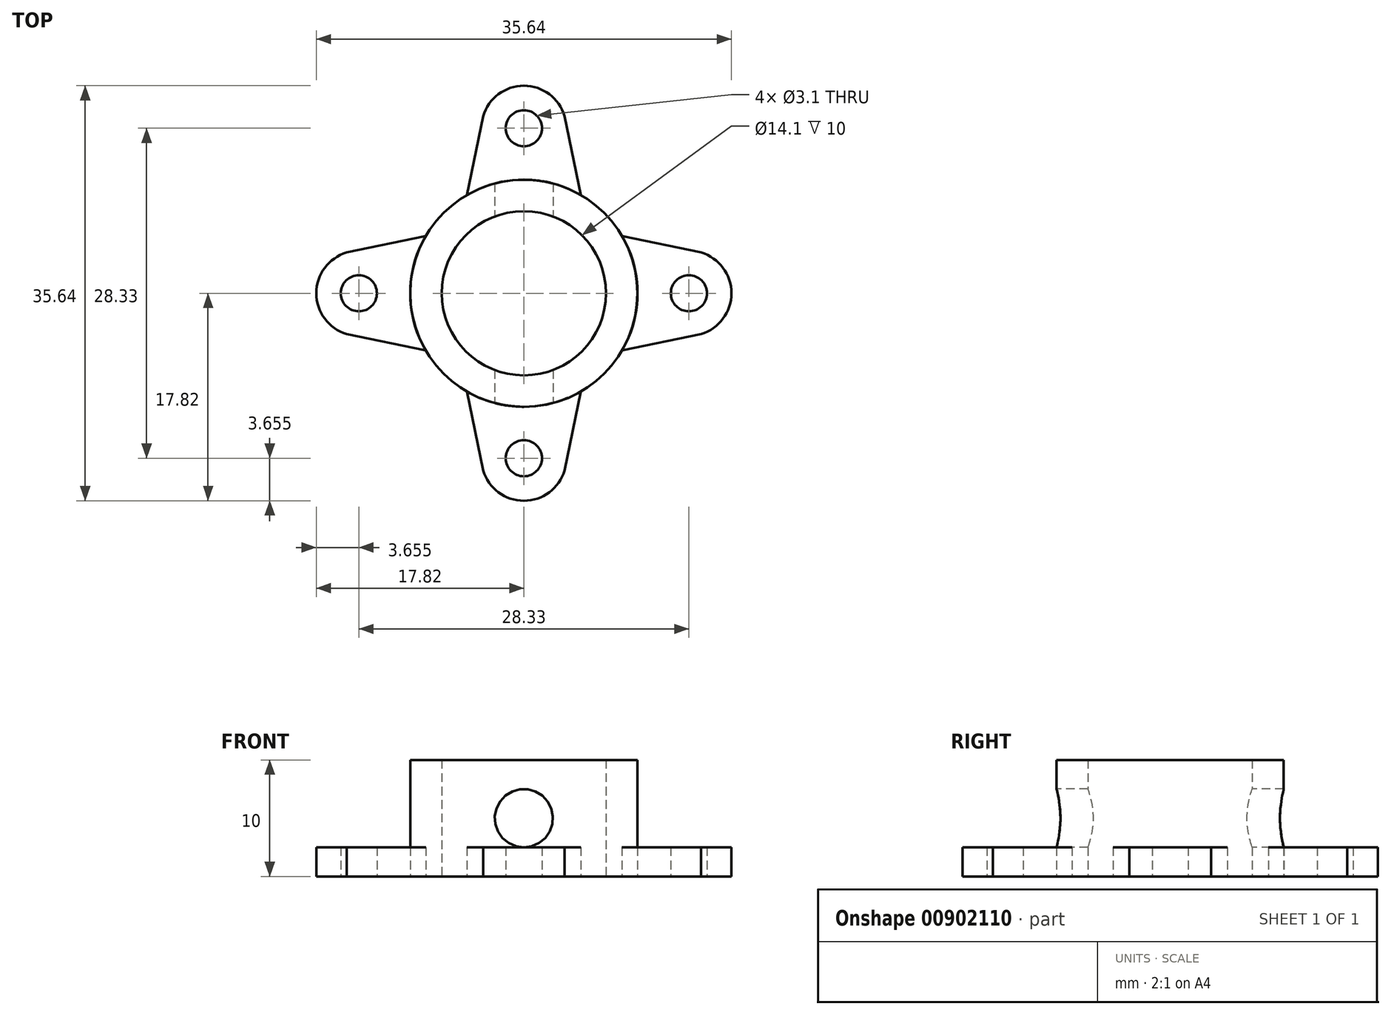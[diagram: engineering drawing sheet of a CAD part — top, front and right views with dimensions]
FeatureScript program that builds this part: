
annotation { "Feature Type Name" : "Feature", "Feature Type Description" : "" }
export const myFeature = defineFeature(function(context is Context, id is Id, definition is map)
    precondition{}
    {
        {
            var Q0;
            Q0=qCreatedBy(makeId("Top.planeOp"),FACE);
            var sketch = newSketch(context, id + "F0", { "sketchPlane" : qUnion([Q0])});
            skCircle(sketch, "E0", {"center": v(0, 0) * mm, "radius": 9.75 * mm});
            skCircle(sketch, "E1", {"center": v(0, 0) * mm, "radius": 7.05 * mm});
            skSolve(sketch);
        }
        {
            var Q0;
            Q0=qCreatedBy(makeId("Top.planeOp"),FACE);
            var sketch = newSketch(context, id + "F1", { "sketchPlane" : qUnion([Q0])});
            skLineSegment(sketch, "E2", {"start": v(0, 0) * mm, "end": v(0, 9.2) * mm, "construction": true});
            skLineSegment(sketch, "E3", {"start": v(0, 9.2) * mm, "end": v(0, 15.2) * mm, "construction": true});
            skPoint(sketch, "E4", {"position": v(0, 15.2) * mm});
            skLineSegment(sketch, "E5", {"start": v(-3.5, 15.2) * mm, "end": v(-4.9, 8.43) * mm});
            skLineSegment(sketch, "E6.MirrorCS", {"start": v(3.5, 15.2) * mm, "end": v(4.9, 8.43) * mm});
            skArc(sketch, "E7", {"start": v(4.9, 8.43) * mm, "mid": v(0, 9.76) * mm, "end": v(-4.9, 8.43) * mm});
            skArc(sketch, "E8", {"start": v(3.5, 15.2) * mm, "mid": v(0, 17.82) * mm, "end": v(-3.5, 15.2) * mm});
            skCircle(sketch, "E9", {"center": v(0, 14.17) * mm, "radius": 1.55 * mm});
            skPoint(sketch, "E10.center", {"position": v(0, 0) * mm});
            skCircle(sketch, "E11.1.0", {"center": v(-14.17, 0) * mm, "radius": 1.55 * mm});
            skArc(sketch, "E11.1.1", {"start": v(-15.2, 3.5) * mm, "mid": v(-17.82, 0) * mm, "end": v(-15.2, -3.5) * mm});
            skLineSegment(sketch, "E11.1.2", {"start": v(-15.2, -3.5) * mm, "end": v(-8.43, -4.9) * mm});
            skArc(sketch, "E11.1.3", {"start": v(-8.43, 4.9) * mm, "mid": v(-9.76, 0) * mm, "end": v(-8.43, -4.9) * mm});
            skLineSegment(sketch, "E11.1.4", {"start": v(-15.2, 3.5) * mm, "end": v(-8.43, 4.9) * mm});
            skCircle(sketch, "E11.2.0", {"center": v(0, -14.17) * mm, "radius": 1.55 * mm});
            skArc(sketch, "E11.2.1", {"start": v(-3.5, -15.2) * mm, "mid": v(0, -17.82) * mm, "end": v(3.5, -15.2) * mm});
            skLineSegment(sketch, "E11.2.2", {"start": v(3.5, -15.2) * mm, "end": v(4.9, -8.43) * mm});
            skArc(sketch, "E11.2.3", {"start": v(-4.9, -8.43) * mm, "mid": v(0, -9.76) * mm, "end": v(4.9, -8.43) * mm});
            skLineSegment(sketch, "E11.2.4", {"start": v(-3.5, -15.2) * mm, "end": v(-4.9, -8.43) * mm});
            skCircle(sketch, "E11.3.0", {"center": v(14.17, 0) * mm, "radius": 1.55 * mm});
            skArc(sketch, "E11.3.1", {"start": v(15.2, -3.5) * mm, "mid": v(17.82, 0) * mm, "end": v(15.2, 3.5) * mm});
            skLineSegment(sketch, "E11.3.2", {"start": v(15.2, 3.5) * mm, "end": v(8.43, 4.9) * mm});
            skArc(sketch, "E11.3.3", {"start": v(8.43, -4.9) * mm, "mid": v(9.76, 0) * mm, "end": v(8.43, 4.9) * mm});
            skLineSegment(sketch, "E11.3.4", {"start": v(15.2, -3.5) * mm, "end": v(8.43, -4.9) * mm});
            skLineSegment(sketch, "E12", {"start": v(0, 14.17) * mm, "end": v(0, -14.17) * mm, "construction": true});
            skLineSegment(sketch, "E13", {"start": v(0.08, 0) * mm, "end": v(14.17, 0) * mm, "construction": true});
            skSolve(sketch);
        }
        {
            var Q0;
            Q0 = qSketchRegion(id + "F1", true);
            extrude(context, id + "F2", {"entities" : qUnion([Q0]), "depth" : 2.5 * mm, "offsetDistance" : 25 * mm});
        }
        {
            var Q0;
            Q0=makeQuery(id+"F0.imprint","IMPRINT",FACE,{"disambiguationData":[TD([[makeQuery(id+"F0.imprint","IMPRINT",EDGE,{"derivedFrom":sQuery(id+"F0.wireOp",EDGE,"E0")}),1.0]])]});
            extrude(context, id + "F3", {"entities" : qUnion([Q0]), "depth" : 10 * mm, "offsetDistance" : 25 * mm});
        }
        {
            var Q0;
            Q0=qCreatedBy(makeId("Front.planeOp"),FACE);
            cPlane(context, id + "F4", {"entities" : qUnion([Q0]), "cplaneType" : CPlaneType.OFFSET, "offset" : 9.75 * mm, "width" : 150 * mm, "height" : 150 * mm});
        }
        {
            var Q0;
            Q0=qCreatedBy(id+"F4.planeOp",FACE);
            var sketch = newSketch(context, id + "F5", { "sketchPlane" : qUnion([Q0])});
            skLineSegment(sketch, "E14", {"start": v(0, 0) * mm, "end": v(0, 5) * mm, "construction": true});
            skPoint(sketch, "E15", {"position": v(0, 5) * mm});
            skCircle(sketch, "E16", {"center": v(0, 5) * mm, "radius": 2.5 * mm});
            skSolve(sketch);
        }
        {
            var Q0;
            Q0=sQuery(id+"F5.wireOp",VERTEX,"E15");
            var Q1;
            Q1=makeQuery(id+"F3.opExtrude","SWEPT_BODY",BODY,{"disambiguationData":[OSD([sQuery(id+"F0.wireOp",EDGE,"E0"),sQuery(id+"F0.wireOp",EDGE,"E1")])]});
            hole(context, id + "F6", {"style" : HoleStyle.SIMPLE, "endStyle" : HoleEndStyle.BLIND, "holeDiameter" : 5 * mm, "majorDiameter" : 5 * mm, "holeDepth" : 19.5 * mm, "isTappedThrough" : true, "tappedDepth" : 12 * mm, "tapClearance" : 3, "startFromSketch" : true, "locations" : qUnion([Q0]), "scope" : qUnion([Q1])});
        }
    });
